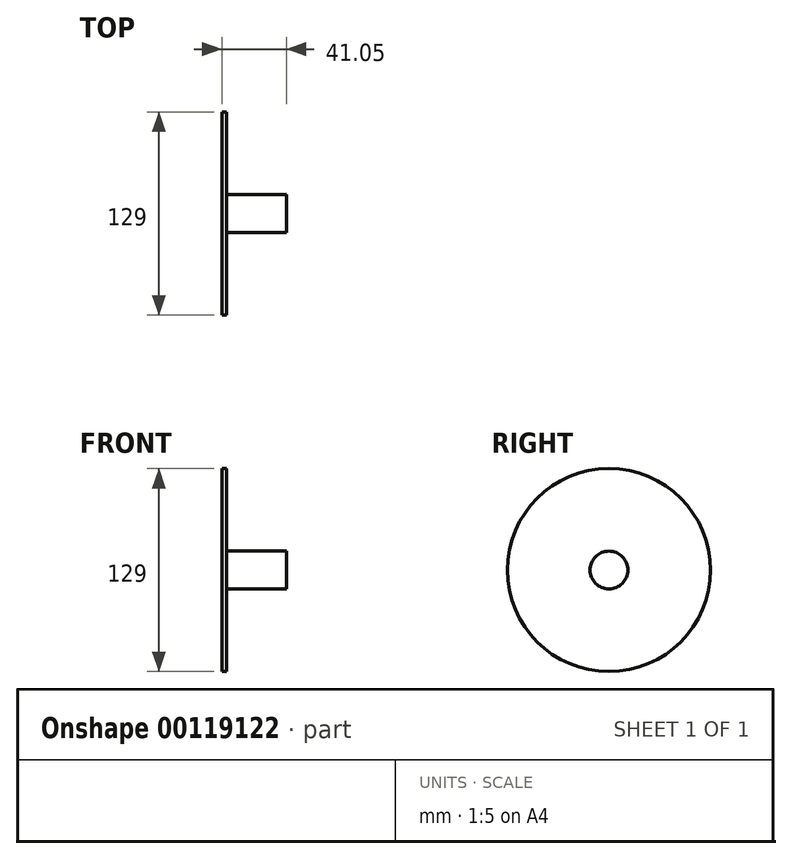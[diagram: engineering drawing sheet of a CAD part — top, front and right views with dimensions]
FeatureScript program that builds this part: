
annotation { "Feature Type Name" : "Feature", "Feature Type Description" : "" }
export const myFeature = defineFeature(function(context is Context, id is Id, definition is map)
    precondition{}
    {
        {
            var Q0;
            Q0=qCreatedBy(makeId("Right.planeOp"),FACE);
            var sketch = newSketch(context, id + "F0", { "sketchPlane" : qUnion([Q0])});
            skCircle(sketch, "E0", {"center": v(0, 0) * mm, "radius": 64.5 * mm});
            skSolve(sketch);
        }
        {
            var Q0;
            Q0=makeQuery(id+"F0.imprint","IMPRINT",FACE,{"disambiguationData":[TD([[makeQuery(id+"F0.imprint","IMPRINT",EDGE,{"derivedFrom":sQuery(id+"F0.wireOp",EDGE,"E0")}),1.0]])]});
            extrude(context, id + "F1", {"entities" : qUnion([Q0]), "depth" : 3 * mm});
        }
        {
            var Q0;
            Q0=makeQuery(id+"F1.opExtrude","CAP_FACE",FACE,{"disambiguationData":[OSD([sQuery(id+"F0.wireOp",EDGE,"E0")])],"isStart":false});
            var sketch = newSketch(context, id + "F2", { "sketchPlane" : qUnion([Q0])});
            skCircle(sketch, "E1", {"center": v(0, 0) * mm, "radius": 12 * mm});
            skSolve(sketch);
        }
        {
            var Q0;
            Q0=makeQuery(id+"F2.imprint","IMPRINT",FACE,{"disambiguationData":[TD([[makeQuery(id+"F2.imprint","IMPRINT",EDGE,{"derivedFrom":sQuery(id+"F2.wireOp",EDGE,"E1")}),1.0]])]});
            extrude(context, id + "F3", {"entities" : qUnion([Q0]), "operationType" : NewBodyOperationType.ADD, "depth" : 19 * mm});
        }
        {
            var Q0;
            Q0=makeQuery(id+"F3.opExtrude","CAP_FACE",FACE,{"disambiguationData":[OSD([sQuery(id+"F2.wireOp",EDGE,"E1")])],"isStart":false});
            var sketch = newSketch(context, id + "F4", { "sketchPlane" : qUnion([Q0])});
            skLineSegment(sketch, "E2", {"start": v(0, 0) * mm, "end": v(-180, 0) * mm, "construction": true});
            skArc(sketch, "E3.0.startCap", {"start": v(0, 12) * mm, "mid": v(12, 0) * mm, "end": v(0, -12) * mm});
            skArc(sketch, "E3.0.endCap", {"start": v(-180, -12) * mm, "mid": v(-192, 0) * mm, "end": v(-180, 12) * mm});
            skLineSegment(sketch, "E3.0.left", {"start": v(0, -12) * mm, "end": v(-180, -12) * mm});
            skLineSegment(sketch, "E3.0.right", {"start": v(0, 12) * mm, "end": v(-180, 12) * mm});
            skLineSegment(sketch, "E4", {"start": v(-180, 0) * mm, "end": v(-192, 0) * mm, "construction": true});
            skSolve(sketch);
        }
        {
            var Q0;
            Q0=makeQuery(id+"F4.imprint","IMPRINT",FACE,{"disambiguationData":[TD([[makeQuery(id+"F4.imprint","IMPRINT",EDGE,{"derivedFrom":sQuery(id+"F4.wireOp",EDGE,"E3.0.endCap")}),-1.0]])]});
            var Q1;
            {var subQ0=sQuery(id+"F4.wireOp",EDGE,"E3.0.startCap");Q1=makeQuery(id+"F4.imprint","IMPRINT",FACE,{"disambiguationData":[TD([[makeQuery(id+"F4.imprint","IMPRINT",EDGE,{"derivedFrom":subQ0}),1.0]])]});}
            extrude(context, id + "F5", {"entities" : qUnion([Q0, Q1]), "operationType" : NewBodyOperationType.ADD, "depth" : 19.05 * mm});
        }
    });
